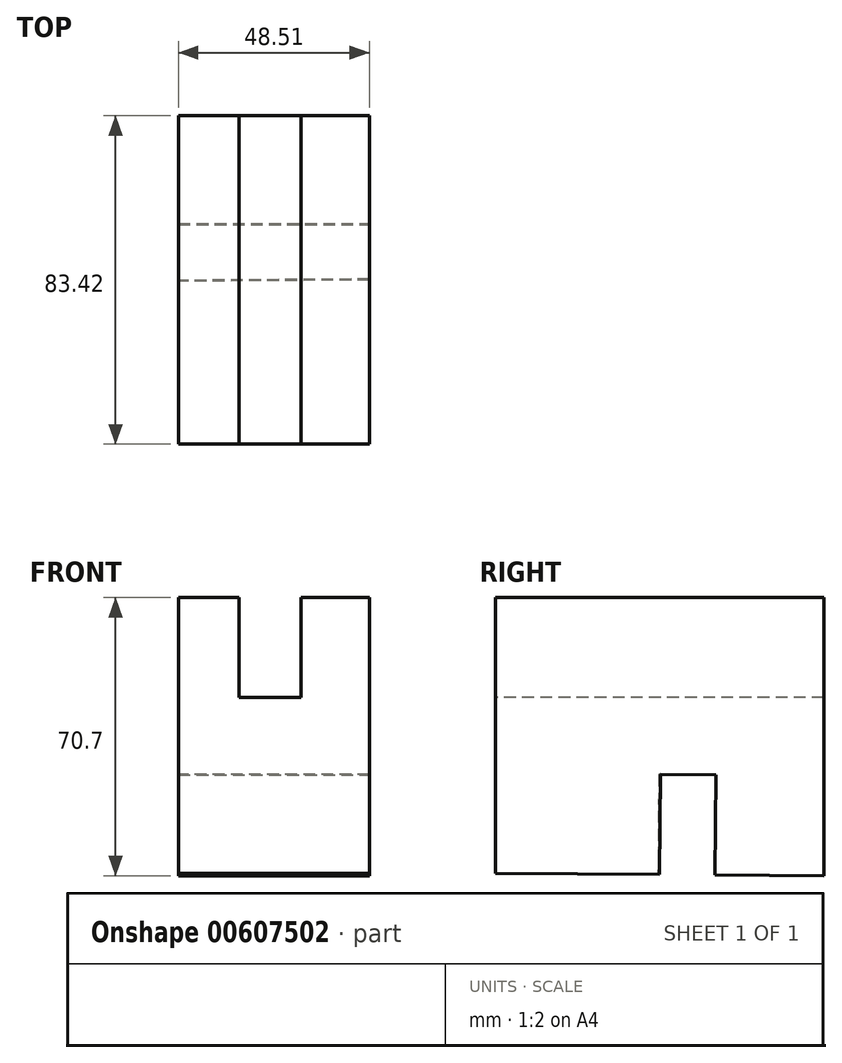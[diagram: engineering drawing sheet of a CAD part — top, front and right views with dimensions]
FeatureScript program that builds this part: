
annotation { "Feature Type Name" : "Feature", "Feature Type Description" : "" }
export const myFeature = defineFeature(function(context is Context, id is Id, definition is map)
    precondition{}
    {
        {
            var Q0;
            Q0=qCreatedBy(makeId("Right.planeOp"),FACE);
            var sketch = newSketch(context, id + "F0", { "sketchPlane" : qUnion([Q0])});
            skLineSegment(sketch, "E0", {"start": v(-41.71, -47.6) * mm, "end": v(-41.71, 22.48) * mm});
            skLineSegment(sketch, "E1", {"start": v(-41.71, 22.48) * mm, "end": v(41.71, 22.48) * mm});
            skLineSegment(sketch, "E2", {"start": v(41.71, 22.48) * mm, "end": v(41.71, -48.22) * mm});
            skLineSegment(sketch, "E3", {"start": v(41.71, -48.22) * mm, "end": v(-41.71, -47.6) * mm});
            skSolve(sketch);
        }
        {
            var Q0;
            Q0 = qSketchRegion(id + "F0", true);
            extrude(context, id + "F1", {"entities" : qUnion([Q0]), "depth" : 48.5 * mm, "offsetDistance" : 25.4 * mm});
        }
        {
            var Q0;
            Q0=makeQuery(id+"F1.opExtrude","SWEPT_FACE",FACE,{"disambiguationData":[OSD([sQuery(id+"F0.wireOp",EDGE,"E1")])]});
            var sketch = newSketch(context, id + "F2", { "sketchPlane" : qUnion([Q0])});
            skLineSegment(sketch, "E4", {"start": v(15.35, 41.71) * mm, "end": v(15.35, -41.71) * mm});
            skLineSegment(sketch, "E5", {"start": v(31.17, 41.71) * mm, "end": v(31.17, -41.71) * mm});
            skLineSegment(sketch, "E6", {"start": v(15.35, 41.71) * mm, "end": v(31.17, 41.71) * mm});
            skLineSegment(sketch, "E7", {"start": v(15.35, -41.71) * mm, "end": v(31.17, -41.71) * mm});
            skSolve(sketch);
        }
        {
            var Q0;
            Q0=makeQuery(id+"F2.imprint","IMPRINT",FACE,{"disambiguationData":[TD([[makeQuery(id+"F2.imprint","IMPRINT",EDGE,{"derivedFrom":sQuery(id+"F2.wireOp",EDGE,"E4")}),1.0]])]});
            extrude(context, id + "F3", {"entities" : qUnion([Q0]), "operationType" : NewBodyOperationType.REMOVE, "oppositeDirection" : true, "depth" : 25.4 * mm, "offsetDistance" : 25.4 * mm});
        }
        {
            var Q0;
            Q0=makeQuery(id+"F1.opExtrude","SWEPT_FACE",FACE,{"disambiguationData":[OSD([sQuery(id+"F0.wireOp",EDGE,"E3")])]});
            var sketch = newSketch(context, id + "F4", { "sketchPlane" : qUnion([Q0])});
            skLineSegment(sketch, "E8", {"start": v(48.51, -0.36) * mm, "end": v(0, 0) * mm});
            skLineSegment(sketch, "E9", {"start": v(0, -14.47) * mm, "end": v(48.51, -14.47) * mm});
            skLineSegment(sketch, "E10", {"start": v(48.51, -0.36) * mm, "end": v(48.51, -14.47) * mm});
            skLineSegment(sketch, "E11", {"start": v(0, -0.36) * mm, "end": v(0, -14.47) * mm});
            skSolve(sketch);
        }
        {
            var Q0;
            {var subQ1=sQuery(id+"F4.wireOp",EDGE,"E8");Q0=makeQuery(id+"F4.imprint","IMPRINT",FACE,{"disambiguationData":[TD([[makeQuery(id+"F4.imprint","IMPRINT",EDGE,{"derivedFrom":subQ1}),1.0]])]});}
            extrude(context, id + "F5", {"entities" : qUnion([Q0]), "operationType" : NewBodyOperationType.REMOVE, "oppositeDirection" : true, "depth" : 25.4 * mm, "offsetDistance" : 25.4 * mm});
        }
    });
